FCSTD DOCUMENT  (FreeCAD 0.19R0.19.2)
Label: laptopStand012
License: All rights reserved
LicenseURL: http://en.wikipedia.org/wiki/All_rights_reserved
objects: Sketcher::SketchObject×1
note: 1 computed .brp shape members not serialized (recipe doc carries the construction recipe); baked Part::Feature solids carry a one-line shape summary decoded from their .brp

FEATURE [Sketcher::SketchObject] Sketch
  FullyConstrained = true
  sketch-geometry (12):
    g0: LineSegment StartX=-22.9272 StartY=136.221 StartZ=0 EndX=-22.9272 EndY=-103.779 EndZ=0
    g1: LineSegment StartX=-22.9272 StartY=136.221 StartZ=0 EndX=387.073 EndY=136.221 EndZ=0
    g2: LineSegment StartX=-22.9272 StartY=-103.779 StartZ=0 EndX=387.073 EndY=-103.779 EndZ=0
    g3: LineSegment StartX=387.073 StartY=136.221 StartZ=0 EndX=387.073 EndY=-103.779 EndZ=0
    g4: LineSegment StartX=-10.9272 StartY=124.221 StartZ=0 EndX=-10.9272 EndY=115.221 EndZ=0
    g5: LineSegment StartX=-10.9272 StartY=124.221 StartZ=0 EndX=-1.92719 EndY=124.221 EndZ=0
    g6: LineSegment StartX=-10.9272 StartY=-91.7794 StartZ=0 EndX=-10.9272 EndY=-82.7794 EndZ=0
    g7: LineSegment StartX=-10.9272 StartY=-91.7794 StartZ=0 EndX=-1.92719 EndY=-91.7794 EndZ=0
    g8: LineSegment StartX=375.073 StartY=-91.7794 StartZ=0 EndX=366.073 EndY=-91.7794 EndZ=0
    g9: LineSegment StartX=375.073 StartY=-91.7794 StartZ=0 EndX=375.073 EndY=-82.7794 EndZ=0
    g10: LineSegment StartX=375.073 StartY=124.221 StartZ=0 EndX=366.073 EndY=124.221 EndZ=0
    g11: LineSegment StartX=375.073 StartY=124.221 StartZ=0 EndX=375.073 EndY=115.221 EndZ=0
  constraints (38):
    c: Vertical(g0)
    c: Distance(g0) = 240
    c: Horizontal(g1)
    c: Distance(g1) = 410
    c: Coincident(g1,g0)
    c: Coincident(g2,g0)
    c: Horizontal(g2)
    c: Coincident(g3,g1)
    c: Vertical(g3)
    c: Coincident(g2,g3)
    c: Block(g1)
    c: Vertical(g4)
    c: Distance(g4) = 9
    c: Block(g4)
    c: Coincident(g5,g4)
    c: Horizontal(g5)
    c: Distance(g5) = 9
    c: Block(g5)
    c: Vertical(g6)
    c: Distance(g6) = 9
    c: Block(g6)
    c: Coincident(g7,g6)
    c: Horizontal(g7)
    c: Distance(g7) = 9
    c: Horizontal(g8)
    c: Distance(g8) = 9
    c: Block(g8)
    c: Coincident(g9,g8)
    c: Vertical(g9)
    c: Distance(g9) = 9
    c: Block(g9)
    c: Horizontal(g10)
    c: Distance(g10) = 9
    c: Block(g10)
    c: Coincident(g11,g10)
    c: Vertical(g11)
    c: Distance(g11) = 9
    c: Block(g11)
